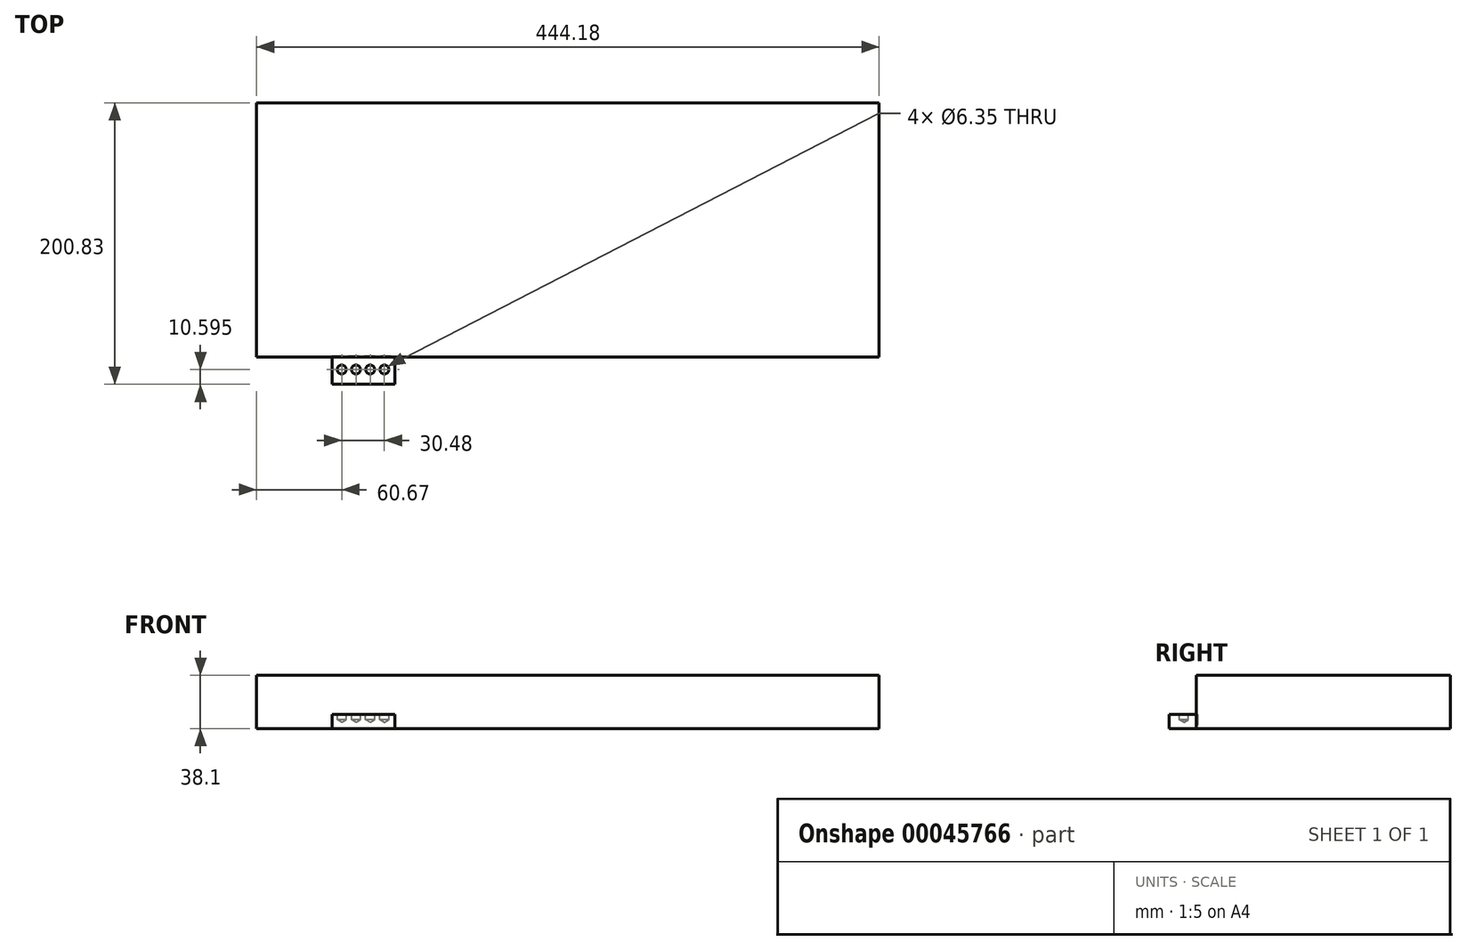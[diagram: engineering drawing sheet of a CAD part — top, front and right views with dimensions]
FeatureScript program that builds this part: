
annotation { "Feature Type Name" : "Feature", "Feature Type Description" : "" }
export const myFeature = defineFeature(function(context is Context, id is Id, definition is map)
    precondition{}
    {
        {
            var Q0;
            Q0=qCreatedBy(makeId("Top.planeOp"),FACE);
            var sketch = newSketch(context, id + "F0", { "sketchPlane" : qUnion([Q0])});
            skLineSegment(sketch, "E0.bottom", {"start": v(-202.3, 80.97) * mm, "end": v(241.88, 80.97) * mm});
            skLineSegment(sketch, "E0.top", {"start": v(-202.3, -100.31) * mm, "end": v(241.88, -100.31) * mm});
            skLineSegment(sketch, "E0.left", {"start": v(-202.3, 80.97) * mm, "end": v(-202.3, -100.31) * mm});
            skLineSegment(sketch, "E0.right", {"start": v(241.88, 80.97) * mm, "end": v(241.88, -100.31) * mm});
            skSolve(sketch);
        }
        {
            var Q0;
            Q0=makeQuery(id+"F0.imprint","IMPRINT",FACE,{"disambiguationData":[TD([[makeQuery(id+"F0.imprint","IMPRINT",EDGE,{"derivedFrom":sQuery(id+"F0.wireOp",EDGE,"E0.bottom")}),-1.0]])]});
            extrude(context, id + "F1", {"entities" : qUnion([Q0]), "depth" : 38.1 * mm});
        }
        {
            var Q0;
            Q0=qCreatedBy(makeId("Top.planeOp"),FACE);
            var sketch = newSketch(context, id + "F2", { "sketchPlane" : qUnion([Q0])});
            skLineSegment(sketch, "E1.bottom", {"start": v(-148.44, -99.55) * mm, "end": v(-103.68, -99.55) * mm});
            skLineSegment(sketch, "E1.top", {"start": v(-148.44, -119.86) * mm, "end": v(-103.68, -119.86) * mm});
            skLineSegment(sketch, "E1.left", {"start": v(-148.44, -99.55) * mm, "end": v(-148.44, -119.86) * mm});
            skLineSegment(sketch, "E1.right", {"start": v(-103.68, -99.55) * mm, "end": v(-103.68, -119.86) * mm});
            skSolve(sketch);
        }
        {
            var Q0;
            Q0 = qSketchRegion(id + "F2", true);
            extrude(context, id + "F3", {"entities" : qUnion([Q0]), "depth" : 10.16 * mm});
        }
        {
            var Q0;
            Q0=makeQuery(id+"F3.opExtrude","CAP_FACE",FACE,{"disambiguationData":[OSD([sQuery(id+"F2.wireOp",EDGE,"E1.bottom"),sQuery(id+"F2.wireOp",EDGE,"E1.top"),sQuery(id+"F2.wireOp",EDGE,"E1.left"),sQuery(id+"F2.wireOp",EDGE,"E1.right")])],"isStart":false});
            var sketch = newSketch(context, id + "F4", { "sketchPlane" : qUnion([Q0])});
            skCircle(sketch, "E2", {"center": v(-141.63, -109.27) * mm, "radius": 4.36 * mm});
            skCircle(sketch, "E3.1.0.0", {"center": v(-131.47, -109.27) * mm, "radius": 4.36 * mm});
            skCircle(sketch, "E3.2.0.0", {"center": v(-121.3, -109.27) * mm, "radius": 4.36 * mm});
            skCircle(sketch, "E3.3.0.0", {"center": v(-111.15, -109.27) * mm, "radius": 4.36 * mm});
            skLineSegment(sketch, "E3.direction1", {"start": v(-141.63, -109.27) * mm, "end": v(-131.47, -109.27) * mm, "construction": true});
            skSolve(sketch);
        }
        {
            var Q0;
            Q0=sQuery(id+"F4.wireOp",VERTEX,"E3.direction1.start");
            var Q1;
            Q1=sQuery(id+"F4.wireOp",VERTEX,"E3.1.0.0.center");
            var Q2;
            Q2=sQuery(id+"F4.wireOp",VERTEX,"E3.2.0.0.center");
            var Q3;
            Q3=sQuery(id+"F4.wireOp",VERTEX,"E3.3.0.0.center");
            var Q4;
            Q4=makeQuery(id+"F3.opExtrude","SWEPT_BODY",BODY,{"disambiguationData":[OSD([sQuery(id+"F2.wireOp",EDGE,"E1.bottom"),sQuery(id+"F2.wireOp",EDGE,"E1.top"),sQuery(id+"F2.wireOp",EDGE,"E1.left"),sQuery(id+"F2.wireOp",EDGE,"E1.right")])]});
            hole(context, id + "F5", {"style" : HoleStyle.SIMPLE, "holeDiameter" : 6.35 * mm, "endStyle" : HoleEndStyle.BLIND, "holeDepth" : 3.8 * mm, "locations" : qUnion([Q0, Q1, Q2, Q3]), "scope" : qUnion([Q4])});
        }
    });
